# Revit family: E SONNIGER - HEATER CONDENS - CR ONE, CR1, CR2, CR3, CR3 MAX, CR4 MAX
name_source: partatom
category: Wyposażenie mechaniczne
revit_build: Autodesk Revit 2018 (Build: 20170927_1515(x64)
units: mm (PartAtom-declared; Revit-internal decimal feet)

## family parameters
Klasyfikacja = Brak
Obiekt nadrzędny = Powierzchnia
Punkt obliczania pomieszczeń = Nie
Tnij formami wycięć po wczytaniu = Nie
Typ części = Normalny
Współdzielony = Nie
Wymiar okrągłego złącza = Użyj średnicy

## types (14) — shared parameters
Domyślna rzędna = 1219.200 mm
IP class protection = IP54
O = 130.000 mm
Opis = Water heater
Producent = SONNIGER Polska Sp. z o.o. Sp. k.
material = 230,230,230
max temperature of the water agent = 120 °C
max working pressure = 1600000.0 Pa
power supply voltage = 230 V
zero-valued in all types: noise level

## per-type parameters (varying)
| type | H | Model | O1 | S g | W g | heat output max. | max air output | maximum air range | min heat output | motor power | motor speed | n° of unit rows | operating noise level: speed I 41 dB(A) / speed II 50 db(A) / speed 3 59 db(A) | weight with water | weight without water | ΔT |
| CR ONE - wall mounting | 18536.143 mm | Heater CONDENS CR ONE | Tak | 13120.000 mm | 13850.000 mm | 25 kW | 1600.0 m³/h | 14000.000 mm | 5 kW | 124 W | 1400 | 2 | speed I 35 dB(A) / speed II 46 dB(A) / speed III 52 dB(A) | 10.70 kg | 9.60 kg | 25 °C |
| CR1 - wall mounting | 26136.143 mm | Heater CONDENS CR1 | Tak | 16000.000 mm | 16000.000 mm | 35 kW | 3900.0 m³/h | 24000.000 mm | 10 kW | 250 W | 1350 | 1 | speed I 44 dB(A) / speed II 52 dB(A) / speed III 62 dB(A) | 11.90 kg | 10.80 kg | 13 °C |
| CR2 - wall mounting | 24536.143 mm | Heater CONDENS CR2 | Tak | 15900.000 mm | 15100.000 mm | 50 kW | 3350.0 m³/h | 21000.000 mm | 15 kW | 250 W | 1350 | 2 | speed I 41 dB(A) / speed II 50 dB(A) / speed III 60 dB(A) | 14.80 kg | 12.70 kg | 22 °C |
| CR3 - wall mounting | 22936.143 mm | Heater CONDENS CR3 | Tak | 15400.000 mm | 14600.000 mm | 70 kW | 2950.0 m³/h | 19000.000 mm | 20 kW | 250 W | 1350 | 3 | speed I 39 dB(A) / speed II 48 dB(A) / speed III 58 dB(A) | 16.90 kg | 14.50 kg | 34 °C |
| CR ONE - ceiling mounting | 9536.143 mm | Heater CONDENS CR ONE | Tak | 9100.000 mm | 9900.000 mm | 25 kW | 1600.0 m³/h | 14000.000 mm | 5 kW | 124 W | 1400 | 2 | speed I 35 dB(A) / speed II 46 dB(A) / speed III 52 dB(A) | 10.70 kg | 9.60 kg | 25 °C |
| CR1 - ceiling mounting | 12536.143 mm | Heater CONDENS CR1 | Tak | 11420.000 mm | 10510.000 mm | 35 kW | 3900.0 m³/h | 24000.000 mm | 10 kW | 250 W | 1350 | 1 | speed I 44 dB(A) / speed II 52 dB(A) / speed III 62 dB(A) | 11.90 kg | 10.80 kg | 13 °C |
| CR2 - ceiling mounting | 11836.143 mm | Heater CONDENS CR2 | Tak | 10900.000 mm | 10360.000 mm | 50 kW | 3350.0 m³/h | 21000.000 mm | 15 kW | 250 W | 1350 | 2 | speed I 41 dB(A) / speed II 50 dB(A) / speed III 60 dB(A) | 14.80 kg | 12.70 kg | 22 °C |
| CR3 - ceiling mounting | 11036.143 mm | Heater CONDENS CR3 | Tak | 10760.000 mm | 9760.000 mm | 70 kW | 2950.0 m³/h | 19000.000 mm | 20 kW | 250 W | 1350 | 3 | speed I 39 dB(A) / speed II 48 dB(A) / speed III 58 dB(A) | 16.90 kg | 14.50 kg | 34 °C |
| CR2 MAX - ceiling mounting | 14860.341 mm | Heater CONDENS CR2 MAX | Nie | 12470.000 mm | 11470.000 mm | 70 kW | 5700.0 m³/h | 26000.000 mm | 25 kW | 520 W | 1380 | 2 | speed I 41 dB(A) / speed II 50 dB(A) / speed III 59 dB(A) | 25.20 kg | 23.60 kg | 22 °C |
| CR2 MAX - wall mounting | 13536.341 mm | Heater CONDENS CR2 MAX | Nie | 19500.000 mm | 19500.000 mm | 70 kW | 5700.0 m³/h | 26000.000 mm | 25 kW | 520 W | 1380 | 2 | speed I 41 dB(A) / speed II 50 dB(A) / speed III 59 dB(A) | 25.20 kg | 23.60 kg | 22 °C |
| CR3 MAX - ceiling mounting | 14060.341 mm | Heater CONDENS CR3 MAX | Nie | 12000.000 mm | 11250.000 mm | 95 kW | 5600.0 m³/h | 25000.000 mm | 35 kW | 520 W | 1380 | 3 | speed I 40 dB(A) / speed II 48 dB(A) / speed III 58 dB(A) | 27.40 kg | 25.20 kg | 35 °C |
| CR3 MAX - wall mounting | 31160.341 mm | Heater CONDENS CR3 MAX | Nie | 17900.000 mm | 17100.000 mm | 95 kW | 5600.0 m³/h | 25000.000 mm | 35 kW | 520 W | 1380 | 3 | speed I 40 dB(A) / speed II 48 dB(A) / speed III 58 dB(A) | 27.40 kg | 25.50 kg | 35 °C |
| CR4 MAX - ceiling mounting | 13360.341 mm | Heater CONDENS CR4 MAX | Nie | 11820.000 mm | 10830.000 mm | 120 kW | 5100.0 m³/h | 23000.000 mm | 40 kW | 520 W | 1380 | 3 | speed I 40 dB(A) / speed II 48 dB(A) / speed III 58 dB(A) | 28.00 kg | 25.50 kg | 44 °C |
| CR4 MAX - wall mounting | 32860.341 mm | Heater CONDENS CR4 MAX | Nie | 18400.000 mm | 17550.000 mm | 120 kW | 5100.0 m³/h | 23000.000 mm | 40 kW | 520 W | 1380 | 3 | speed I 40 dB(A) / speed II 48 dB(A) / speed III 58 dB(A) | 28.00 kg | 25.50 kg | 44 °C |
